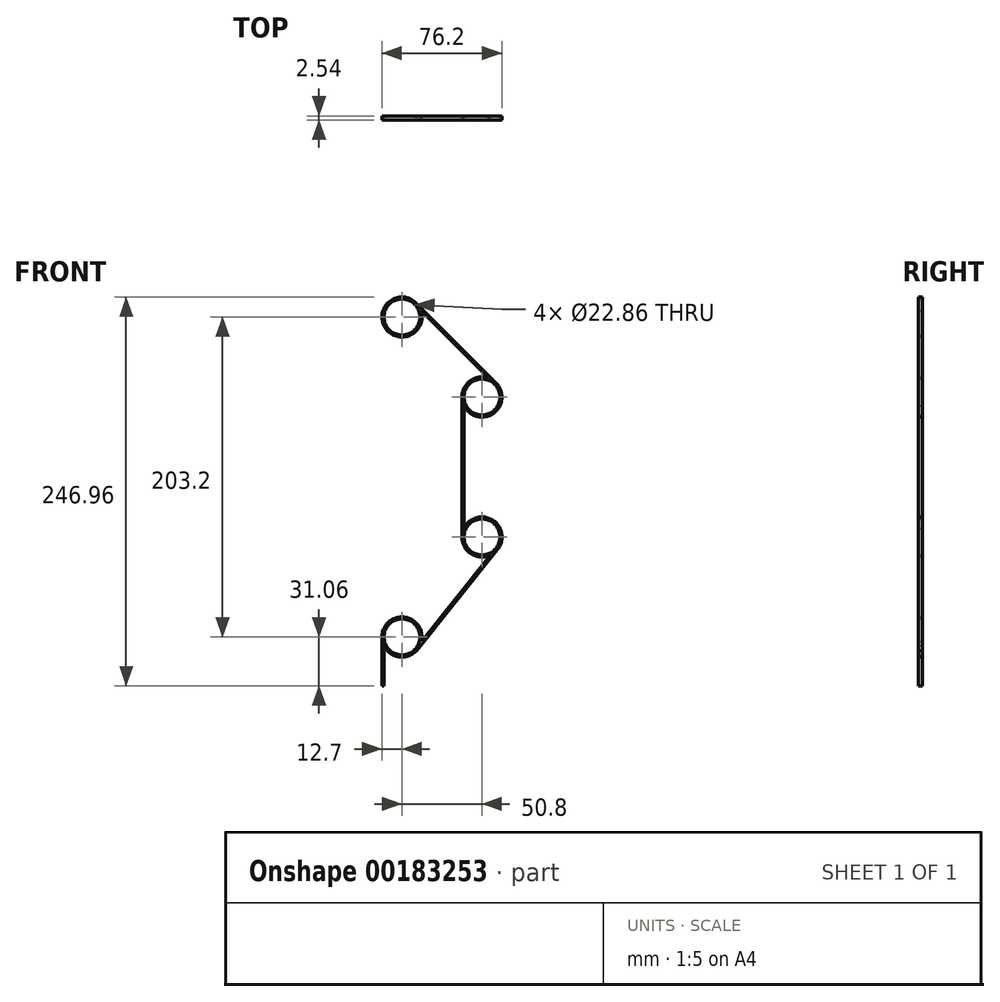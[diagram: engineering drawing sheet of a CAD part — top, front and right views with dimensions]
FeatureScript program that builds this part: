
annotation { "Feature Type Name" : "Feature", "Feature Type Description" : "" }
export const myFeature = defineFeature(function(context is Context, id is Id, definition is map)
    precondition{}
    {
        {
            var Q0;
            Q0=qCreatedBy(makeId("Front.planeOp"),FACE);
            var sketch = newSketch(context, id + "F0", { "sketchPlane" : qUnion([Q0])});
            skCircle(sketch, "E0", {"center": v(0, 0) * mm, "radius": 11.43 * mm});
            skArc(sketch, "E1", {"start": v(12.38, -2.82) * mm, "mid": v(1.42, 12.62) * mm, "end": v(-12.7, 0) * mm});
            skCircle(sketch, "E2", {"center": v(50.8, 63.5) * mm, "radius": 11.43 * mm});
            skArc(sketch, "E3", {"start": v(38.1, 63.5) * mm, "mid": v(44.02, 52.76) * mm, "end": v(56.27, 52.04) * mm});
            skCircle(sketch, "E4", {"center": v(50.8, 152.4) * mm, "radius": 11.43 * mm});
            skArc(sketch, "E5", {"start": v(54.97, 164.4) * mm, "mid": v(43.44, 162.75) * mm, "end": v(38.1, 152.4) * mm});
            skCircle(sketch, "E6", {"center": v(0, 203.2) * mm, "radius": 11.43 * mm});
            skArc(sketch, "E7", {"start": v(8.98, 212.18) * mm, "mid": v(-10.76, 196.46) * mm, "end": v(12, 207.37) * mm});
            skLineSegment(sketch, "E8", {"start": v(-12.7, 0) * mm, "end": v(-12.7, -31.06) * mm});
            skLineSegment(sketch, "E9", {"start": v(-11.43, -5.54) * mm, "end": v(-11.43, -31.06) * mm});
            skLineSegment(sketch, "E10", {"start": v(12.38, -2.82) * mm, "end": v(56.27, 52.04) * mm});
            skLineSegment(sketch, "E11", {"start": v(60.71, 55.56) * mm, "end": v(9.19, -8.77) * mm});
            skLineSegment(sketch, "E12.left", {"start": v(38.1, 152.4) * mm, "end": v(38.1, 63.5) * mm});
            skLineSegment(sketch, "E12.right", {"start": v(39.37, 146.86) * mm, "end": v(39.37, 69.04) * mm});
            skLineSegment(sketch, "E13", {"start": v(59.78, 161.38) * mm, "end": v(8.98, 212.18) * mm});
            skLineSegment(sketch, "E14", {"start": v(12, 207.37) * mm, "end": v(54.97, 164.4) * mm});
            skArc(sketch, "E15.trimOffspring", {"start": v(39.37, 146.86) * mm, "mid": v(58.16, 142.05) * mm, "end": v(59.78, 161.38) * mm});
            skPoint(sketch, "E16.orphan", {"position": v(39.37, 63.5) * mm});
            skArc(sketch, "E17.trimOffspring", {"start": v(60.71, 55.56) * mm, "mid": v(57.58, 74.24) * mm, "end": v(39.37, 69.04) * mm});
            skLineSegment(sketch, "E18", {"start": v(-12.7, -31.06) * mm, "end": v(-11.43, -31.06) * mm});
            skArc(sketch, "E19.trimOffspring", {"start": v(-11.43, -5.54) * mm, "mid": v(-1.97, -12.55) * mm, "end": v(9.19, -8.77) * mm});
            skPoint(sketch, "E20.orphan", {"position": v(-11.43, 0) * mm});
            skSolve(sketch);
        }
        {
            var Q0;
            Q0=makeQuery(id+"F0.imprint","IMPRINT",FACE,{"disambiguationData":[TD([[makeQuery(id+"F0.imprint","IMPRINT",EDGE,{"derivedFrom":sQuery(id+"F0.wireOp",EDGE,"E0")}),-1.0]])]});
            extrude(context, id + "F1", {"entities" : qUnion([Q0]), "depth" : 2.54 * mm});
        }
    });
